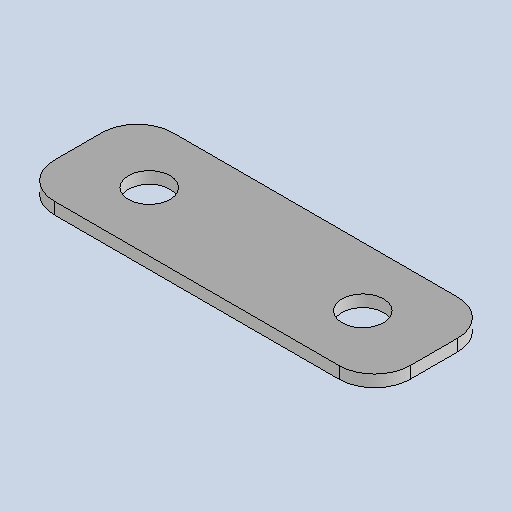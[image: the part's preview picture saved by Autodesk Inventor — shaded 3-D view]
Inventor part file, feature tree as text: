
AUTODESK INVENTOR PART (.ipt)
format: ipt  version: 2025.3 (Build 293356030, 356C)  size: 135,168 bytes
history: native  units: mm
features: other x2, sheet_metal_op x1, chamfer x1, sketch x1
ambient origin geometry x8: Origin, YZ Plane, XZ Plane, XY Plane, X Axis, Y Axis, Z Axis, Center Point
bodies: Solid1 (feature_tree)
feature tree (5):
  sheet_metal_op  "Face1"
  chamfer  "Corner Round1"
  sketch  "Sketch1"  dims[d0=60.0mm d1=20.0mm d2=7.0mm d3=36.0mm d4=2.0mm d5=6.0mm]
  other  "Plate1"
  other  "Definition1"
